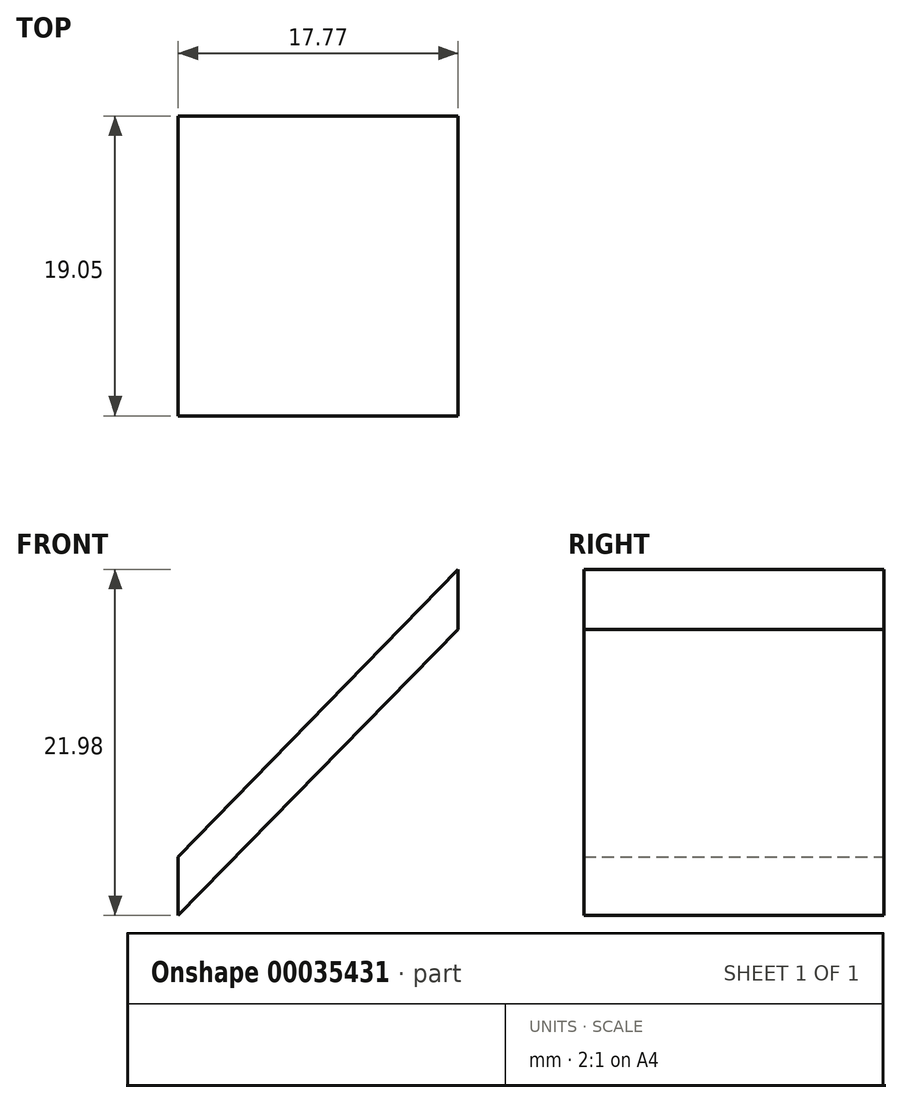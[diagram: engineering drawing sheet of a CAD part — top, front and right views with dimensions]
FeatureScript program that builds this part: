
annotation { "Feature Type Name" : "Feature", "Feature Type Description" : "" }
export const myFeature = defineFeature(function(context is Context, id is Id, definition is map)
    precondition{}
    {
        {
            var Q0;
            Q0=qCreatedBy(makeId("Front.planeOp"),FACE);
            var sketch = newSketch(context, id + "F0", { "sketchPlane" : qUnion([Q0])});
            skLineSegment(sketch, "E0", {"start": v(0, 0) * mm, "end": v(17.77, 18.25) * mm});
            skLineSegment(sketch, "E1", {"start": v(17.77, 18.25) * mm, "end": v(17.77, 14.42) * mm});
            skLineSegment(sketch, "E2", {"start": v(17.77, 14.42) * mm, "end": v(0, -3.73) * mm});
            skLineSegment(sketch, "E3", {"start": v(0, -3.73) * mm, "end": v(0, 0) * mm});
            skSolve(sketch);
        }
        {
            var Q0;
            Q0 = qSketchRegion(id + "F0", true);
            extrude(context, id + "F1", {"entities" : qUnion([Q0]), "depth" : 19.05 * mm});
        }
        {
            var Q0;
            Q0=makeQuery(id+"F1.opExtrude","SWEPT_BODY",BODY,{"disambiguationData":[OSD([sQuery(id+"F0.wireOp",EDGE,"E0"),sQuery(id+"F0.wireOp",EDGE,"E1"),sQuery(id+"F0.wireOp",EDGE,"E2"),sQuery(id+"F0.wireOp",EDGE,"E3")])]});
            transform(context, id + "F2", {"entities" : qUnion([Q0]), "transformType" : TransformType.TRANSLATION_3D, "dx" : 0 * mm, "dy" : 0 * mm, "dz" : 0 * mm, "makeCopy" : true});
        }
        {
            var Q0;
            Q0=makeQuery(id+"F2.opPattern","COPY",BODY,{"derivedFrom":makeQuery(id+"F1.opExtrude","SWEPT_BODY",BODY,{"disambiguationData":[OSD([sQuery(id+"F0.wireOp",EDGE,"E0"),sQuery(id+"F0.wireOp",EDGE,"E1"),sQuery(id+"F0.wireOp",EDGE,"E2"),sQuery(id+"F0.wireOp",EDGE,"E3")])]}),"instanceName":"1"});
            deleteBodies(context, id + "F3", {"entities" : qUnion([Q0])});
        }
    });
